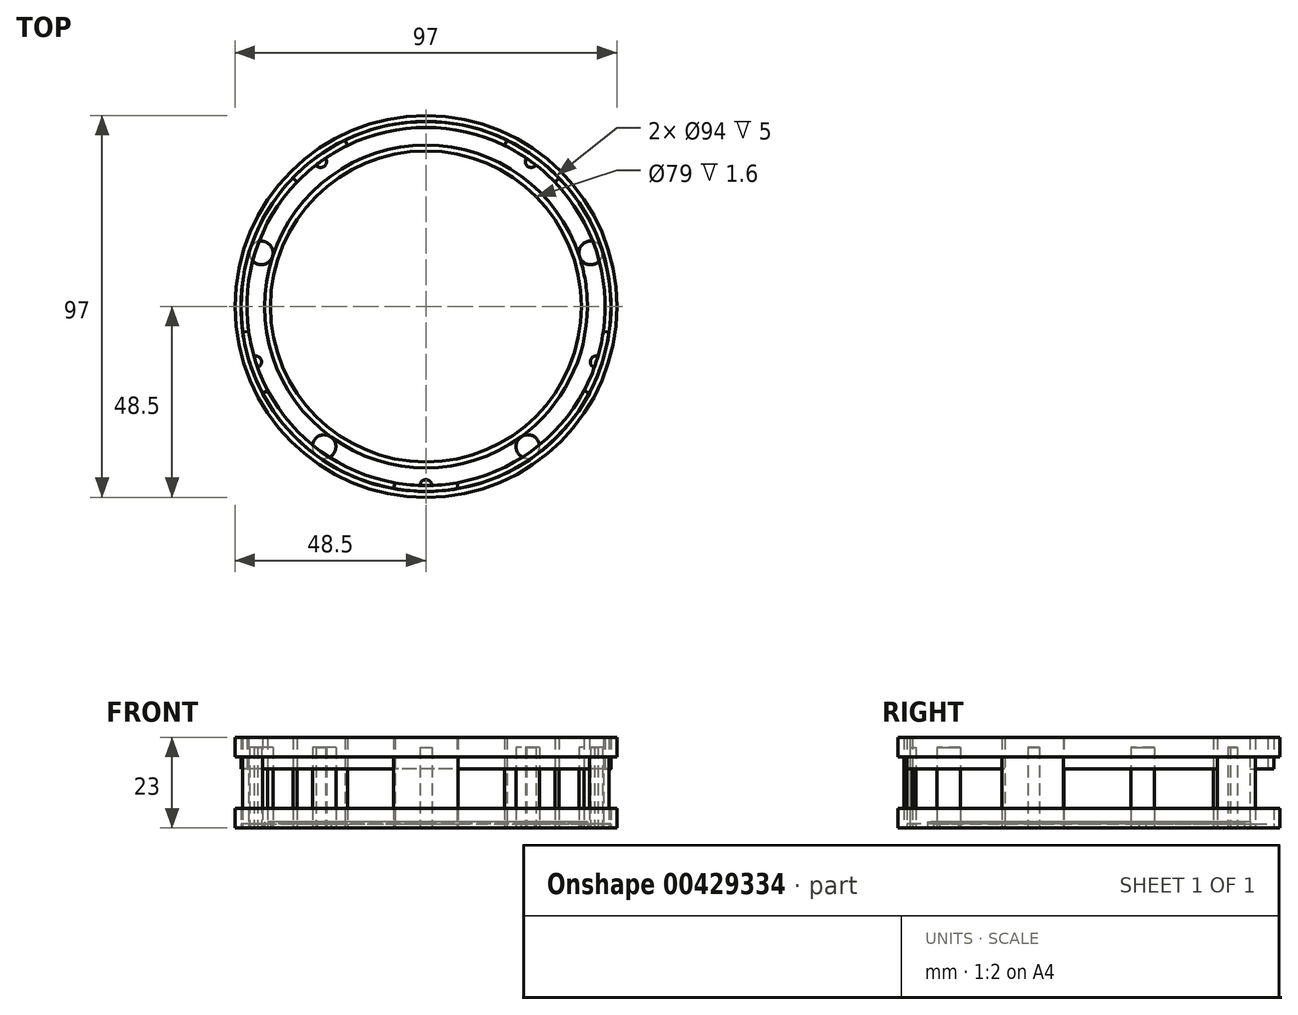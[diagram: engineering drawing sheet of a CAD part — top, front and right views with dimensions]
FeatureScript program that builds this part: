
annotation { "Feature Type Name" : "Feature", "Feature Type Description" : "" }
export const myFeature = defineFeature(function(context is Context, id is Id, definition is map)
    precondition{}
    {
        {
            var Q0;
            Q0=qCreatedBy(makeId("Top.planeOp"),FACE);
            var sketch = newSketch(context, id + "F0", { "sketchPlane" : qUnion([Q0])});
            skCircle(sketch, "E0", {"center": v(0, 0) * mm, "radius": 48.5 * mm});
            skCircle(sketch, "E1", {"center": v(0, 0) * mm, "radius": 47 * mm});
            skCircle(sketch, "E2", {"center": v(0, 0) * mm, "radius": 41 * mm});
            skCircle(sketch, "E3", {"center": v(0, 0) * mm, "radius": 39.5 * mm});
            skCircle(sketch, "E4", {"center": v(0, 0) * mm, "radius": 44 * mm, "construction": true});
            skLineSegment(sketch, "E5", {"start": v(0, 39.5) * mm, "end": v(0, 48.5) * mm, "construction": true});
            skCircle(sketch, "E6", {"center": v(0, 0) * mm, "radius": 45.5 * mm});
            skCircle(sketch, "E7.1.0", {"center": v(-41.85, 13.6) * mm, "radius": 3 * mm});
            skCircle(sketch, "E7.2.0", {"center": v(-25.86, -35.6) * mm, "radius": 3 * mm});
            skCircle(sketch, "E8.1.3.0", {"center": v(25.86, -35.6) * mm, "radius": 3 * mm});
            skCircle(sketch, "E8.1.4.0", {"center": v(41.85, 13.6) * mm, "radius": 3 * mm});
            skCircle(sketch, "E9.1.0", {"center": v(-26.74, 36.81) * mm, "radius": 1.5 * mm});
            skCircle(sketch, "E9.3.0", {"center": v(-43.27, -14.06) * mm, "radius": 1.5 * mm});
            skCircle(sketch, "E9.5.0", {"center": v(0, -45.5) * mm, "radius": 1.5 * mm});
            skCircle(sketch, "E9.7.0", {"center": v(43.27, -14.06) * mm, "radius": 1.5 * mm});
            skCircle(sketch, "E9.9.0", {"center": v(26.74, 36.81) * mm, "radius": 1.5 * mm});
            skLineSegment(sketch, "E10", {"start": v(0, -45.5) * mm, "end": v(0, -47) * mm});
            skLineSegment(sketch, "E11", {"start": v(0, 0) * mm, "end": v(0, -47) * mm, "construction": true});
            skLineSegment(sketch, "E12", {"start": v(-7.9, -44.8) * mm, "end": v(-8.16, -46.29) * mm});
            skLineSegment(sketch, "E13", {"start": v(7.9, -44.8) * mm, "end": v(8.16, -46.29) * mm});
            skLineSegment(sketch, "E14.1.0", {"start": v(40.17, -21.36) * mm, "end": v(41.5, -22.07) * mm});
            skLineSegment(sketch, "E14.1.1", {"start": v(45.06, -6.33) * mm, "end": v(46.54, -6.54) * mm});
            skLineSegment(sketch, "E14.2.0", {"start": v(32.73, 31.6) * mm, "end": v(33.8, 32.65) * mm});
            skLineSegment(sketch, "E14.2.1", {"start": v(19.95, 40.9) * mm, "end": v(20.6, 42.24) * mm});
            skLineSegment(sketch, "E14.3.0", {"start": v(-19.95, 40.9) * mm, "end": v(-20.6, 42.24) * mm});
            skLineSegment(sketch, "E14.3.1", {"start": v(-32.73, 31.6) * mm, "end": v(-33.8, 32.65) * mm});
            skLineSegment(sketch, "E14.4.0", {"start": v(-45.06, -6.33) * mm, "end": v(-46.54, -6.54) * mm});
            skLineSegment(sketch, "E14.4.1", {"start": v(-40.17, -21.36) * mm, "end": v(-41.5, -22.07) * mm});
            skSolve(sketch);
        }
        {
            var Q0;
            Q0=makeQuery(id+"F0.imprint","IMPRINT",FACE,{"disambiguationData":[TD([[makeQuery(id+"F0.imprint","IMPRINT",EDGE,{"derivedFrom":sQuery(id+"F0.wireOp",EDGE,"E3")}),1.0]])]});
            var Q1;
            {var subQ7=sQuery(id+"F0.wireOp",EDGE,"E2");var subQ10=sQuery(id+"F0.wireOp",EDGE,"E7.2.0");var subQ12=makeQuery(id+"F0.imprint","INTERSECT",VERTEX,{"derivedFrom":[subQ7,subQ10]});Q1=makeQuery(id+"F0.imprint","IMPRINT",FACE,{"disambiguationData":[TD([[makeQuery(id+"F0.imprint","IMPRINT",EDGE,{"disambiguationData":[TD([[subQ12,-1.0]])],"derivedFrom":subQ7}),-1.0]])]});}
            var Q2;
            {var subQ8=sQuery(id+"F0.wireOp",EDGE,"E8.1.4.0");var subQ9=sQuery(id+"F0.wireOp",EDGE,"E2");var subQ10=makeQuery(id+"F0.imprint","INTERSECT",VERTEX,{"derivedFrom":[subQ9,subQ8]});Q2=makeQuery(id+"F0.imprint","IMPRINT",FACE,{"disambiguationData":[TD([[makeQuery(id+"F0.imprint","IMPRINT",EDGE,{"disambiguationData":[TD([[subQ10,1.0]])],"derivedFrom":subQ9}),-1.0]])]});}
            var Q3;
            {var subQ1=sQuery(id+"F0.wireOp",EDGE,"E2");var subQ5=sQuery(id+"F0.wireOp",EDGE,"E7.1.0");var subQ6=makeQuery(id+"F0.imprint","INTERSECT",VERTEX,{"derivedFrom":[subQ1,subQ5]});Q3=makeQuery(id+"F0.imprint","IMPRINT",FACE,{"disambiguationData":[TD([[makeQuery(id+"F0.imprint","IMPRINT",EDGE,{"disambiguationData":[TD([[subQ6,1.0]])],"derivedFrom":subQ1}),-1.0]])]});}
            var Q4;
            {var subQ5=sQuery(id+"F0.wireOp",EDGE,"E2");var subQ10=sQuery(id+"F0.wireOp",EDGE,"E7.1.0");var subQ12=makeQuery(id+"F0.imprint","INTERSECT",VERTEX,{"derivedFrom":[subQ5,subQ10]});Q4=makeQuery(id+"F0.imprint","IMPRINT",FACE,{"disambiguationData":[TD([[makeQuery(id+"F0.imprint","IMPRINT",EDGE,{"disambiguationData":[TD([[subQ12,-1.0]])],"derivedFrom":subQ5}),-1.0]])]});}
            var Q5;
            {var subQ0=sQuery(id+"F0.wireOp",EDGE,"E12");Q5=makeQuery(id+"F0.imprint","IMPRINT",FACE,{"disambiguationData":[TD([[makeQuery(id+"F0.imprint","IMPRINT",EDGE,{"derivedFrom":subQ0}),-1.0]])]});}
            var Q6;
            {var subQ0=sQuery(id+"F0.wireOp",EDGE,"E14.4.1");Q6=makeQuery(id+"F0.imprint","IMPRINT",FACE,{"disambiguationData":[TD([[makeQuery(id+"F0.imprint","IMPRINT",EDGE,{"derivedFrom":subQ0}),1.0]])]});}
            var Q7;
            {var subQ0=sQuery(id+"F0.wireOp",EDGE,"E13");Q7=makeQuery(id+"F0.imprint","IMPRINT",FACE,{"disambiguationData":[TD([[makeQuery(id+"F0.imprint","IMPRINT",EDGE,{"derivedFrom":subQ0}),1.0]])]});}
            var Q8;
            {var subQ0=sQuery(id+"F0.wireOp",EDGE,"E14.1.0");Q8=makeQuery(id+"F0.imprint","IMPRINT",FACE,{"disambiguationData":[TD([[makeQuery(id+"F0.imprint","IMPRINT",EDGE,{"derivedFrom":subQ0}),-1.0]])]});}
            var Q9;
            {var subQ0=sQuery(id+"F0.wireOp",EDGE,"E14.1.1");Q9=makeQuery(id+"F0.imprint","IMPRINT",FACE,{"disambiguationData":[TD([[makeQuery(id+"F0.imprint","IMPRINT",EDGE,{"derivedFrom":subQ0}),1.0]])]});}
            var Q10;
            {var subQ0=sQuery(id+"F0.wireOp",EDGE,"E14.2.0");Q10=makeQuery(id+"F0.imprint","IMPRINT",FACE,{"disambiguationData":[TD([[makeQuery(id+"F0.imprint","IMPRINT",EDGE,{"derivedFrom":subQ0}),-1.0]])]});}
            var Q11;
            {var subQ0=sQuery(id+"F0.wireOp",EDGE,"E14.2.1");Q11=makeQuery(id+"F0.imprint","IMPRINT",FACE,{"disambiguationData":[TD([[makeQuery(id+"F0.imprint","IMPRINT",EDGE,{"derivedFrom":subQ0}),1.0]])]});}
            var Q12;
            {var subQ0=sQuery(id+"F0.wireOp",EDGE,"E14.3.1");Q12=makeQuery(id+"F0.imprint","IMPRINT",FACE,{"disambiguationData":[TD([[makeQuery(id+"F0.imprint","IMPRINT",EDGE,{"derivedFrom":subQ0}),1.0]])]});}
            var Q13;
            {var subQ0=sQuery(id+"F0.wireOp",EDGE,"E14.4.0");Q13=makeQuery(id+"F0.imprint","IMPRINT",FACE,{"disambiguationData":[TD([[makeQuery(id+"F0.imprint","IMPRINT",EDGE,{"derivedFrom":subQ0}),-1.0]])]});}
            extrude(context, id + "F1", {"entities" : qUnion([Q0, Q1, Q2, Q3, Q4, Q5, Q6, Q7, Q8, Q9, Q10, Q11, Q12, Q13]), "depth" : 1 * mm});
        }
        {
            var Q0;
            Q0=makeQuery(id+"F0.imprint","IMPRINT",FACE,{"disambiguationData":[TD([[makeQuery(id+"F0.imprint","IMPRINT",EDGE,{"derivedFrom":sQuery(id+"F0.wireOp",EDGE,"E3")}),-1.0]])]});
            extrude(context, id + "F2", {"entities" : qUnion([Q0]), "depth" : 1.6 * mm});
        }
        {
            var Q0;
            {var subQ0=sQuery(id+"F0.wireOp",EDGE,"E7.1.0");var subQ1=sQuery(id+"F0.wireOp",EDGE,"E6");var subQ2=makeQuery(id+"F0.imprint","INTERSECT",VERTEX,{"disambiguationData":[OD(0.0)],"derivedFrom":[subQ1,subQ0]});Q0=makeQuery(id+"F0.imprint","IMPRINT",FACE,{"disambiguationData":[TD([[makeQuery(id+"F0.imprint","IMPRINT",EDGE,{"disambiguationData":[TD([[subQ2,-1.0]])],"derivedFrom":subQ1}),1.0]])]});}
            var Q1;
            {var subQ0=sQuery(id+"F0.wireOp",EDGE,"E9.3.0");var subQ1=sQuery(id+"F0.wireOp",EDGE,"E6");var subQ2=makeQuery(id+"F0.imprint","INTERSECT",VERTEX,{"disambiguationData":[OD(0.0)],"derivedFrom":[subQ1,subQ0]});Q1=makeQuery(id+"F0.imprint","IMPRINT",FACE,{"disambiguationData":[TD([[makeQuery(id+"F0.imprint","IMPRINT",EDGE,{"disambiguationData":[TD([[subQ2,-1.0]])],"derivedFrom":subQ1}),1.0]])]});}
            var Q2;
            {var subQ0=sQuery(id+"F0.wireOp",EDGE,"E9.1.0");var subQ1=sQuery(id+"F0.wireOp",EDGE,"E6");var subQ2=makeQuery(id+"F0.imprint","INTERSECT",VERTEX,{"disambiguationData":[OD(0.0)],"derivedFrom":[subQ1,subQ0]});Q2=makeQuery(id+"F0.imprint","IMPRINT",FACE,{"disambiguationData":[TD([[makeQuery(id+"F0.imprint","IMPRINT",EDGE,{"disambiguationData":[TD([[subQ2,-1.0]])],"derivedFrom":subQ1}),1.0]])]});}
            var Q3;
            {var subQ0=sQuery(id+"F0.wireOp",EDGE,"E7.2.0");var subQ1=sQuery(id+"F0.wireOp",EDGE,"E6");var subQ2=makeQuery(id+"F0.imprint","INTERSECT",VERTEX,{"disambiguationData":[OD(0.0)],"derivedFrom":[subQ1,subQ0]});Q3=makeQuery(id+"F0.imprint","IMPRINT",FACE,{"disambiguationData":[TD([[makeQuery(id+"F0.imprint","IMPRINT",EDGE,{"disambiguationData":[TD([[subQ2,-1.0]])],"derivedFrom":subQ1}),1.0]])]});}
            var Q4;
            {var subQ0=sQuery(id+"F0.wireOp",EDGE,"E6");var subQ1=makeQuery(id+"F0.imprint","INTERSECT",VERTEX,{"derivedFrom":[subQ0,sQuery(id+"F0.wireOp",EDGE,"E10")]});Q4=makeQuery(id+"F0.imprint","IMPRINT",FACE,{"disambiguationData":[TD([[makeQuery(id+"F0.imprint","IMPRINT",EDGE,{"disambiguationData":[TD([[subQ1,1.0]])],"derivedFrom":subQ0}),1.0]])]});}
            var Q5;
            {var subQ0=sQuery(id+"F0.wireOp",EDGE,"E8.1.3.0");var subQ1=sQuery(id+"F0.wireOp",EDGE,"E6");var subQ2=makeQuery(id+"F0.imprint","INTERSECT",VERTEX,{"disambiguationData":[OD(0.0)],"derivedFrom":[subQ1,subQ0]});Q5=makeQuery(id+"F0.imprint","IMPRINT",FACE,{"disambiguationData":[TD([[makeQuery(id+"F0.imprint","IMPRINT",EDGE,{"disambiguationData":[TD([[subQ2,-1.0]])],"derivedFrom":subQ1}),1.0]])]});}
            var Q6;
            {var subQ0=sQuery(id+"F0.wireOp",EDGE,"E9.7.0");var subQ1=sQuery(id+"F0.wireOp",EDGE,"E6");var subQ2=makeQuery(id+"F0.imprint","INTERSECT",VERTEX,{"disambiguationData":[OD(0.0)],"derivedFrom":[subQ1,subQ0]});Q6=makeQuery(id+"F0.imprint","IMPRINT",FACE,{"disambiguationData":[TD([[makeQuery(id+"F0.imprint","IMPRINT",EDGE,{"disambiguationData":[TD([[subQ2,-1.0]])],"derivedFrom":subQ1}),1.0]])]});}
            var Q7;
            {var subQ0=sQuery(id+"F0.wireOp",EDGE,"E8.1.4.0");var subQ1=sQuery(id+"F0.wireOp",EDGE,"E6");var subQ2=makeQuery(id+"F0.imprint","INTERSECT",VERTEX,{"disambiguationData":[OD(0.0)],"derivedFrom":[subQ1,subQ0]});Q7=makeQuery(id+"F0.imprint","IMPRINT",FACE,{"disambiguationData":[TD([[makeQuery(id+"F0.imprint","IMPRINT",EDGE,{"disambiguationData":[TD([[subQ2,1.0]])],"derivedFrom":subQ1}),1.0]])]});}
            var Q8;
            {var subQ0=sQuery(id+"F0.wireOp",EDGE,"E9.9.0");var subQ1=sQuery(id+"F0.wireOp",EDGE,"E6");var subQ2=makeQuery(id+"F0.imprint","INTERSECT",VERTEX,{"disambiguationData":[OD(0.0)],"derivedFrom":[subQ1,subQ0]});Q8=makeQuery(id+"F0.imprint","IMPRINT",FACE,{"disambiguationData":[TD([[makeQuery(id+"F0.imprint","IMPRINT",EDGE,{"disambiguationData":[TD([[subQ2,-1.0]])],"derivedFrom":subQ1}),1.0]])]});}
            var Q9;
            {var subQ0=sQuery(id+"F0.wireOp",EDGE,"E7.1.0");var subQ1=sQuery(id+"F0.wireOp",EDGE,"E6");var subQ2=makeQuery(id+"F0.imprint","INTERSECT",VERTEX,{"disambiguationData":[OD(0.0)],"derivedFrom":[subQ1,subQ0]});Q9=makeQuery(id+"F0.imprint","IMPRINT",FACE,{"disambiguationData":[TD([[makeQuery(id+"F0.imprint","IMPRINT",EDGE,{"disambiguationData":[TD([[subQ2,-1.0]])],"derivedFrom":subQ1}),-1.0]])]});}
            var Q10;
            {var subQ0=sQuery(id+"F0.wireOp",EDGE,"E8.1.4.0");var subQ1=sQuery(id+"F0.wireOp",EDGE,"E6");var subQ2=makeQuery(id+"F0.imprint","INTERSECT",VERTEX,{"disambiguationData":[OD(0.0)],"derivedFrom":[subQ1,subQ0]});Q10=makeQuery(id+"F0.imprint","IMPRINT",FACE,{"disambiguationData":[TD([[makeQuery(id+"F0.imprint","IMPRINT",EDGE,{"disambiguationData":[TD([[subQ2,1.0]])],"derivedFrom":subQ1}),-1.0]])]});}
            var Q11;
            {var subQ0=sQuery(id+"F0.wireOp",EDGE,"E8.1.3.0");var subQ1=sQuery(id+"F0.wireOp",EDGE,"E6");var subQ2=makeQuery(id+"F0.imprint","INTERSECT",VERTEX,{"disambiguationData":[OD(0.0)],"derivedFrom":[subQ1,subQ0]});Q11=makeQuery(id+"F0.imprint","IMPRINT",FACE,{"disambiguationData":[TD([[makeQuery(id+"F0.imprint","IMPRINT",EDGE,{"disambiguationData":[TD([[subQ2,-1.0]])],"derivedFrom":subQ1}),-1.0]])]});}
            var Q12;
            {var subQ0=sQuery(id+"F0.wireOp",EDGE,"E7.2.0");var subQ1=sQuery(id+"F0.wireOp",EDGE,"E6");var subQ2=makeQuery(id+"F0.imprint","INTERSECT",VERTEX,{"disambiguationData":[OD(0.0)],"derivedFrom":[subQ1,subQ0]});Q12=makeQuery(id+"F0.imprint","IMPRINT",FACE,{"disambiguationData":[TD([[makeQuery(id+"F0.imprint","IMPRINT",EDGE,{"disambiguationData":[TD([[subQ2,-1.0]])],"derivedFrom":subQ1}),-1.0]])]});}
            extrude(context, id + "F3", {"entities" : qUnion([Q0, Q1, Q2, Q3, Q4, Q5, Q6, Q7, Q8, Q9, Q10, Q11, Q12]), "depth" : 20.5 * mm});
        }
        {
            var Q0;
            {var subQ0=sQuery(id+"F0.wireOp",EDGE,"E14.4.1");Q0=makeQuery(id+"F0.imprint","IMPRINT",FACE,{"disambiguationData":[TD([[makeQuery(id+"F0.imprint","IMPRINT",EDGE,{"derivedFrom":subQ0}),-1.0]])]});}
            var Q1;
            {var subQ0=sQuery(id+"F0.wireOp",EDGE,"E9.3.0");var subQ1=sQuery(id+"F0.wireOp",EDGE,"E6");var subQ2=makeQuery(id+"F0.imprint","INTERSECT",VERTEX,{"disambiguationData":[OD(0.0)],"derivedFrom":[subQ1,subQ0]});Q1=makeQuery(id+"F0.imprint","IMPRINT",FACE,{"disambiguationData":[TD([[makeQuery(id+"F0.imprint","IMPRINT",EDGE,{"disambiguationData":[TD([[subQ2,-1.0]])],"derivedFrom":subQ1}),-1.0]])]});}
            var Q2;
            {var subQ0=sQuery(id+"F0.wireOp",EDGE,"E14.4.0");Q2=makeQuery(id+"F0.imprint","IMPRINT",FACE,{"disambiguationData":[TD([[makeQuery(id+"F0.imprint","IMPRINT",EDGE,{"derivedFrom":subQ0}),1.0]])]});}
            var Q3;
            {var subQ0=sQuery(id+"F0.wireOp",EDGE,"E14.3.1");Q3=makeQuery(id+"F0.imprint","IMPRINT",FACE,{"disambiguationData":[TD([[makeQuery(id+"F0.imprint","IMPRINT",EDGE,{"derivedFrom":subQ0}),-1.0]])]});}
            var Q4;
            {var subQ0=sQuery(id+"F0.wireOp",EDGE,"E9.1.0");var subQ1=sQuery(id+"F0.wireOp",EDGE,"E6");var subQ2=makeQuery(id+"F0.imprint","INTERSECT",VERTEX,{"disambiguationData":[OD(0.0)],"derivedFrom":[subQ1,subQ0]});Q4=makeQuery(id+"F0.imprint","IMPRINT",FACE,{"disambiguationData":[TD([[makeQuery(id+"F0.imprint","IMPRINT",EDGE,{"disambiguationData":[TD([[subQ2,-1.0]])],"derivedFrom":subQ1}),-1.0]])]});}
            var Q5;
            {var subQ0=sQuery(id+"F0.wireOp",EDGE,"E14.3.0");Q5=makeQuery(id+"F0.imprint","IMPRINT",FACE,{"disambiguationData":[TD([[makeQuery(id+"F0.imprint","IMPRINT",EDGE,{"derivedFrom":subQ0}),1.0]])]});}
            var Q6;
            {var subQ0=sQuery(id+"F0.wireOp",EDGE,"E9.9.0");var subQ1=sQuery(id+"F0.wireOp",EDGE,"E6");var subQ2=makeQuery(id+"F0.imprint","INTERSECT",VERTEX,{"disambiguationData":[OD(0.0)],"derivedFrom":[subQ1,subQ0]});Q6=makeQuery(id+"F0.imprint","IMPRINT",FACE,{"disambiguationData":[TD([[makeQuery(id+"F0.imprint","IMPRINT",EDGE,{"disambiguationData":[TD([[subQ2,-1.0]])],"derivedFrom":subQ1}),-1.0]])]});}
            var Q7;
            {var subQ0=sQuery(id+"F0.wireOp",EDGE,"E14.2.1");Q7=makeQuery(id+"F0.imprint","IMPRINT",FACE,{"disambiguationData":[TD([[makeQuery(id+"F0.imprint","IMPRINT",EDGE,{"derivedFrom":subQ0}),-1.0]])]});}
            var Q8;
            {var subQ0=sQuery(id+"F0.wireOp",EDGE,"E14.2.0");Q8=makeQuery(id+"F0.imprint","IMPRINT",FACE,{"disambiguationData":[TD([[makeQuery(id+"F0.imprint","IMPRINT",EDGE,{"derivedFrom":subQ0}),1.0]])]});}
            var Q9;
            {var subQ0=sQuery(id+"F0.wireOp",EDGE,"E9.7.0");var subQ1=sQuery(id+"F0.wireOp",EDGE,"E6");var subQ2=makeQuery(id+"F0.imprint","INTERSECT",VERTEX,{"disambiguationData":[OD(0.0)],"derivedFrom":[subQ1,subQ0]});Q9=makeQuery(id+"F0.imprint","IMPRINT",FACE,{"disambiguationData":[TD([[makeQuery(id+"F0.imprint","IMPRINT",EDGE,{"disambiguationData":[TD([[subQ2,-1.0]])],"derivedFrom":subQ1}),-1.0]])]});}
            var Q10;
            {var subQ0=sQuery(id+"F0.wireOp",EDGE,"E14.1.1");Q10=makeQuery(id+"F0.imprint","IMPRINT",FACE,{"disambiguationData":[TD([[makeQuery(id+"F0.imprint","IMPRINT",EDGE,{"derivedFrom":subQ0}),-1.0]])]});}
            var Q11;
            {var subQ0=sQuery(id+"F0.wireOp",EDGE,"E14.1.0");Q11=makeQuery(id+"F0.imprint","IMPRINT",FACE,{"disambiguationData":[TD([[makeQuery(id+"F0.imprint","IMPRINT",EDGE,{"derivedFrom":subQ0}),1.0]])]});}
            var Q12;
            {var subQ0=sQuery(id+"F0.wireOp",EDGE,"E10");Q12=makeQuery(id+"F0.imprint","IMPRINT",FACE,{"disambiguationData":[TD([[makeQuery(id+"F0.imprint","IMPRINT",EDGE,{"derivedFrom":subQ0}),-1.0]])]});}
            var Q13;
            {var subQ0=sQuery(id+"F0.wireOp",EDGE,"E10");Q13=makeQuery(id+"F0.imprint","IMPRINT",FACE,{"disambiguationData":[TD([[makeQuery(id+"F0.imprint","IMPRINT",EDGE,{"derivedFrom":subQ0}),1.0]])]});}
            var Q14;
            {var subQ3=sQuery(id+"F0.wireOp",EDGE,"E13");Q14=makeQuery(id+"F0.imprint","IMPRINT",FACE,{"disambiguationData":[TD([[makeQuery(id+"F0.imprint","IMPRINT",EDGE,{"derivedFrom":subQ3}),-1.0]])]});}
            var Q15;
            {var subQ3=sQuery(id+"F0.wireOp",EDGE,"E12");Q15=makeQuery(id+"F0.imprint","IMPRINT",FACE,{"disambiguationData":[TD([[makeQuery(id+"F0.imprint","IMPRINT",EDGE,{"derivedFrom":subQ3}),1.0]])]});}
            extrude(context, id + "F4", {"entities" : qUnion([Q0, Q1, Q2, Q3, Q4, Q5, Q6, Q7, Q8, Q9, Q10, Q11, Q12, Q13, Q14, Q15]), "depth" : 23 * mm});
        }
        {
            var Q0;
            {var subQ0=sQuery(id+"F0.wireOp",EDGE,"E7.1.0");var subQ1=sQuery(id+"F0.wireOp",EDGE,"E6");var subQ2=makeQuery(id+"F0.imprint","INTERSECT",VERTEX,{"disambiguationData":[OD(0.0)],"derivedFrom":[subQ1,subQ0]});Q0=makeQuery(id+"F0.imprint","IMPRINT",FACE,{"disambiguationData":[TD([[makeQuery(id+"F0.imprint","IMPRINT",EDGE,{"disambiguationData":[TD([[subQ2,-1.0]])],"derivedFrom":subQ1}),-1.0]])]});}
            var Q1;
            {var subQ0=sQuery(id+"F0.wireOp",EDGE,"E14.3.1");Q1=makeQuery(id+"F0.imprint","IMPRINT",FACE,{"disambiguationData":[TD([[makeQuery(id+"F0.imprint","IMPRINT",EDGE,{"derivedFrom":subQ0}),1.0]])]});}
            var Q2;
            {var subQ0=sQuery(id+"F0.wireOp",EDGE,"E14.4.0");Q2=makeQuery(id+"F0.imprint","IMPRINT",FACE,{"disambiguationData":[TD([[makeQuery(id+"F0.imprint","IMPRINT",EDGE,{"derivedFrom":subQ0}),-1.0]])]});}
            var Q3;
            {var subQ0=sQuery(id+"F0.wireOp",EDGE,"E7.2.0");var subQ1=sQuery(id+"F0.wireOp",EDGE,"E6");var subQ2=makeQuery(id+"F0.imprint","INTERSECT",VERTEX,{"disambiguationData":[OD(0.0)],"derivedFrom":[subQ1,subQ0]});Q3=makeQuery(id+"F0.imprint","IMPRINT",FACE,{"disambiguationData":[TD([[makeQuery(id+"F0.imprint","IMPRINT",EDGE,{"disambiguationData":[TD([[subQ2,-1.0]])],"derivedFrom":subQ1}),-1.0]])]});}
            var Q4;
            {var subQ0=sQuery(id+"F0.wireOp",EDGE,"E14.4.1");Q4=makeQuery(id+"F0.imprint","IMPRINT",FACE,{"disambiguationData":[TD([[makeQuery(id+"F0.imprint","IMPRINT",EDGE,{"derivedFrom":subQ0}),1.0]])]});}
            var Q5;
            {var subQ0=sQuery(id+"F0.wireOp",EDGE,"E12");Q5=makeQuery(id+"F0.imprint","IMPRINT",FACE,{"disambiguationData":[TD([[makeQuery(id+"F0.imprint","IMPRINT",EDGE,{"derivedFrom":subQ0}),-1.0]])]});}
            var Q6;
            {var subQ0=sQuery(id+"F0.wireOp",EDGE,"E8.1.3.0");var subQ1=sQuery(id+"F0.wireOp",EDGE,"E6");var subQ2=makeQuery(id+"F0.imprint","INTERSECT",VERTEX,{"disambiguationData":[OD(0.0)],"derivedFrom":[subQ1,subQ0]});Q6=makeQuery(id+"F0.imprint","IMPRINT",FACE,{"disambiguationData":[TD([[makeQuery(id+"F0.imprint","IMPRINT",EDGE,{"disambiguationData":[TD([[subQ2,-1.0]])],"derivedFrom":subQ1}),-1.0]])]});}
            var Q7;
            {var subQ0=sQuery(id+"F0.wireOp",EDGE,"E14.1.0");Q7=makeQuery(id+"F0.imprint","IMPRINT",FACE,{"disambiguationData":[TD([[makeQuery(id+"F0.imprint","IMPRINT",EDGE,{"derivedFrom":subQ0}),-1.0]])]});}
            var Q8;
            {var subQ0=sQuery(id+"F0.wireOp",EDGE,"E13");Q8=makeQuery(id+"F0.imprint","IMPRINT",FACE,{"disambiguationData":[TD([[makeQuery(id+"F0.imprint","IMPRINT",EDGE,{"derivedFrom":subQ0}),1.0]])]});}
            var Q9;
            {var subQ0=sQuery(id+"F0.wireOp",EDGE,"E8.1.4.0");var subQ1=sQuery(id+"F0.wireOp",EDGE,"E6");var subQ2=makeQuery(id+"F0.imprint","INTERSECT",VERTEX,{"disambiguationData":[OD(0.0)],"derivedFrom":[subQ1,subQ0]});Q9=makeQuery(id+"F0.imprint","IMPRINT",FACE,{"disambiguationData":[TD([[makeQuery(id+"F0.imprint","IMPRINT",EDGE,{"disambiguationData":[TD([[subQ2,1.0]])],"derivedFrom":subQ1}),-1.0]])]});}
            var Q10;
            {var subQ0=sQuery(id+"F0.wireOp",EDGE,"E14.2.0");Q10=makeQuery(id+"F0.imprint","IMPRINT",FACE,{"disambiguationData":[TD([[makeQuery(id+"F0.imprint","IMPRINT",EDGE,{"derivedFrom":subQ0}),-1.0]])]});}
            var Q11;
            {var subQ0=sQuery(id+"F0.wireOp",EDGE,"E14.1.1");Q11=makeQuery(id+"F0.imprint","IMPRINT",FACE,{"disambiguationData":[TD([[makeQuery(id+"F0.imprint","IMPRINT",EDGE,{"derivedFrom":subQ0}),1.0]])]});}
            var Q12;
            {var subQ0=sQuery(id+"F0.wireOp",EDGE,"E14.2.1");Q12=makeQuery(id+"F0.imprint","IMPRINT",FACE,{"disambiguationData":[TD([[makeQuery(id+"F0.imprint","IMPRINT",EDGE,{"derivedFrom":subQ0}),1.0]])]});}
            extrude(context, id + "F5", {"entities" : qUnion([Q0, Q1, Q2, Q3, Q4, Q5, Q6, Q7, Q8, Q9, Q10, Q11, Q12]), "depth" : 23 * mm, "hasSecondDirection" : true, "secondDirectionOppositeDirection" : true, "secondDirectionDepth" : -15 * mm});
        }
        {
            var Q0;
            Q0=makeQuery(id+"F0.imprint","IMPRINT",FACE,{"disambiguationData":[TD([[makeQuery(id+"F0.imprint","IMPRINT",EDGE,{"derivedFrom":sQuery(id+"F0.wireOp",EDGE,"E0")}),1.0]])]});
            extrude(context, id + "F6", {"entities" : qUnion([Q0]), "depth" : 5 * mm});
        }
        {
            var Q0;
            Q0=makeQuery(id+"F0.imprint","IMPRINT",FACE,{"disambiguationData":[TD([[makeQuery(id+"F0.imprint","IMPRINT",EDGE,{"derivedFrom":sQuery(id+"F0.wireOp",EDGE,"E0")}),1.0]])]});
            extrude(context, id + "F7", {"entities" : qUnion([Q0]), "depth" : 23 * mm, "hasSecondDirection" : true, "secondDirectionOppositeDirection" : true, "secondDirectionDepth" : -18 * mm});
        }
    });
